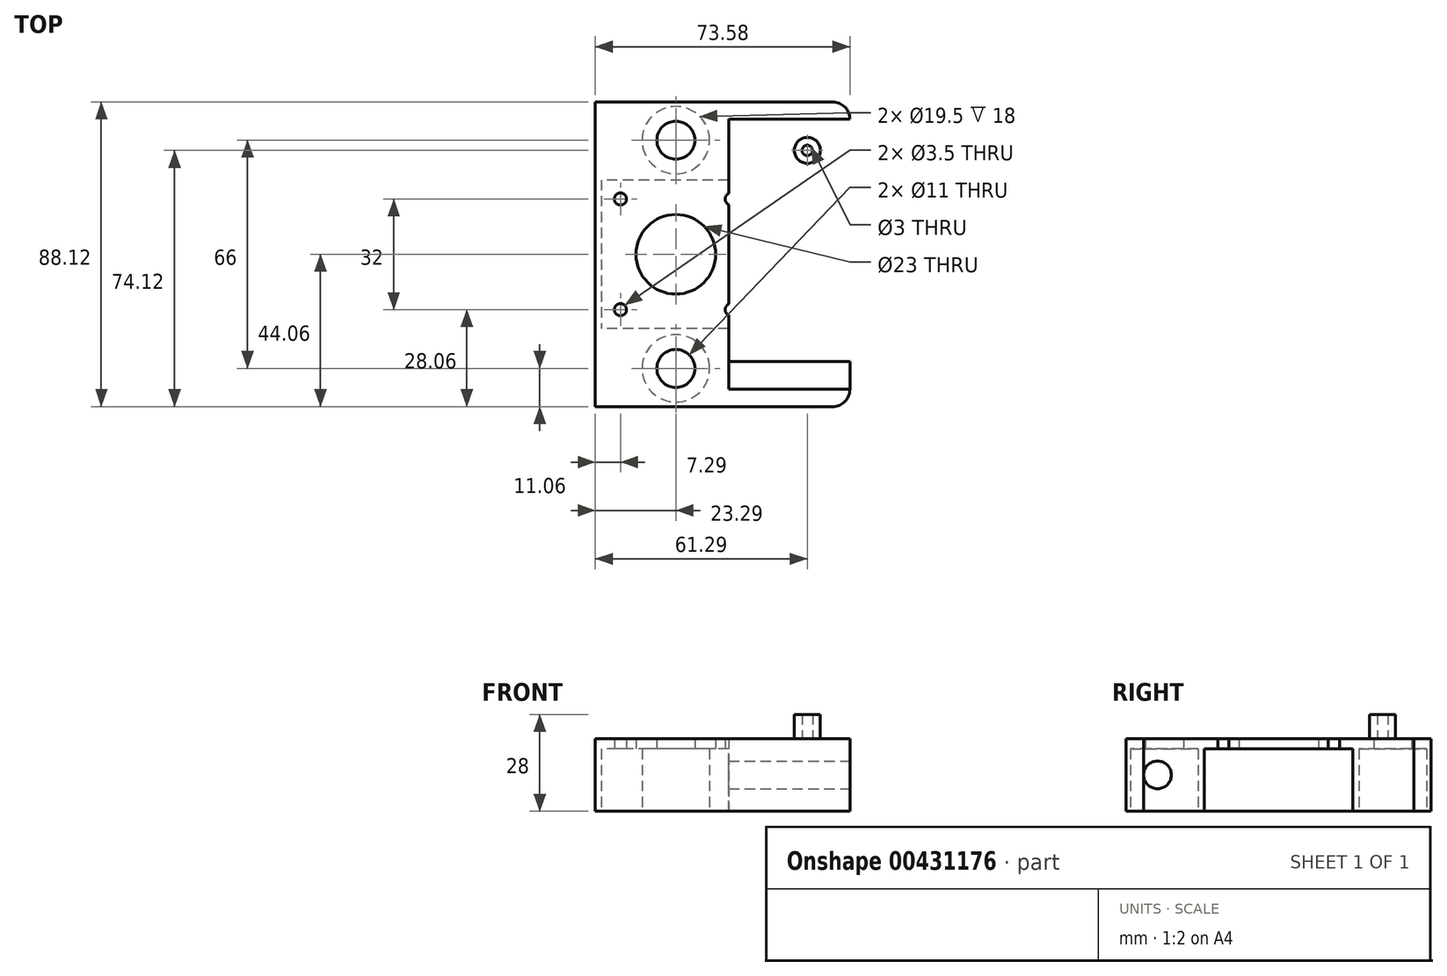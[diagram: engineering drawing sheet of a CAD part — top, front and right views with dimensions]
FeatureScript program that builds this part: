
annotation { "Feature Type Name" : "Feature", "Feature Type Description" : "" }
export const myFeature = defineFeature(function(context is Context, id is Id, definition is map)
    precondition{}
    {
        {
            var Q0;
            Q0=qCreatedBy(makeId("Top.planeOp"),FACE);
            var sketch = newSketch(context, id + "F0", { "sketchPlane" : qUnion([Q0])});
            skLineSegment(sketch, "E0", {"start": v(26.75, 0) * mm, "end": v(38, 0) * mm});
            skCircle(sketch, "E1", {"center": v(38, 0) * mm, "radius": 11.25 * mm});
            skLineSegment(sketch, "E2", {"start": v(0, 0) * mm, "end": v(0, 33) * mm});
            skLineSegment(sketch, "E3", {"start": v(0, 0) * mm, "end": v(0, -33) * mm});
            skLineSegment(sketch, "E4.bottom", {"start": v(0, 27) * mm, "end": v(0, 27) * mm});
            skLineSegment(sketch, "E4.top", {"start": v(0, -27) * mm, "end": v(0, -27) * mm});
            skCircle(sketch, "E5", {"center": v(0, -33) * mm, "radius": 9.75 * mm});
            skCircle(sketch, "E6", {"center": v(0, 33) * mm, "radius": 9.75 * mm});
            skLineSegment(sketch, "E7", {"start": v(0, 0) * mm, "end": v(26.75, 0) * mm});
            skLineSegment(sketch, "E8.bottom", {"start": v(21.5, 21.5) * mm, "end": v(21.48, 21.5) * mm});
            skLineSegment(sketch, "E8.top", {"start": v(21.5, -21.5) * mm, "end": v(-21.5, -21.5) * mm});
            skLineSegment(sketch, "E8.left", {"start": v(21.5, 21.5) * mm, "end": v(21.5, 0) * mm});
            skLineSegment(sketch, "E8.right", {"start": v(-21.5, 21.5) * mm, "end": v(-21.5, -21.5) * mm});
            skPoint(sketch, "E8.middle", {"position": v(0, 0) * mm});
            skLineSegment(sketch, "E9", {"start": v(21.5, 0) * mm, "end": v(21.5, -21.5) * mm});
            skLineSegment(sketch, "E10.bottom", {"start": v(23.3, 44.06) * mm, "end": v(-23.3, 44.06) * mm});
            skLineSegment(sketch, "E10.top", {"start": v(23.3, -44.06) * mm, "end": v(-23.3, -44.06) * mm});
            skLineSegment(sketch, "E10.right", {"start": v(-23.3, 44.06) * mm, "end": v(-23.3, -44.06) * mm});
            skLineSegment(sketch, "E11", {"start": v(21.48, 21.5) * mm, "end": v(-21.5, 21.5) * mm});
            skLineSegment(sketch, "E12.right", {"start": v(50.3, 23.56) * mm, "end": v(50.3, -23.56) * mm});
            skLineSegment(sketch, "E13.bottom", {"start": v(-23.3, 44.06) * mm, "end": v(23.3, 44.06) * mm});
            skLineSegment(sketch, "E13.top", {"start": v(-23.3, -44.06) * mm, "end": v(23.3, -44.06) * mm});
            skCircle(sketch, "E14", {"center": v(0, 33) * mm, "radius": 5.5 * mm});
            skCircle(sketch, "E15", {"center": v(0, -33) * mm, "radius": 5.5 * mm});
            skLineSegment(sketch, "E16", {"start": v(23.3, -44.06) * mm, "end": v(45.3, -44.06) * mm});
            skLineSegment(sketch, "E17", {"start": v(50.3, -39.06) * mm, "end": v(50.3, -23.56) * mm});
            skLineSegment(sketch, "E18", {"start": v(23.3, 44.06) * mm, "end": v(45.3, 44.06) * mm});
            skLineSegment(sketch, "E19", {"start": v(50.3, 39.06) * mm, "end": v(50.3, 23.56) * mm});
            skPoint(sketch, "E20.visualSharp", {"position": v(50.3, -44.06) * mm});
            skArc(sketch, "E20.filletArc", {"start": v(45.3, -44.06) * mm, "mid": v(48.83, -42.6) * mm, "end": v(50.3, -39.06) * mm});
            skPoint(sketch, "E21.visualSharp", {"position": v(50.3, 44.06) * mm});
            skArc(sketch, "E21.filletArc", {"start": v(50.3, 39.06) * mm, "mid": v(48.83, 42.6) * mm, "end": v(45.3, 44.06) * mm});
            skSolve(sketch);
        }
        {
            var Q0;
            Q0=makeQuery(id+"F0.imprint","IMPRINT",FACE,{"disambiguationData":[TD([[makeQuery(id+"F0.imprint","IMPRINT",EDGE,{"derivedFrom":sQuery(id+"F0.wireOp",EDGE,"E1")}),-1.0]])]});
            var Q1;
            Q1=makeQuery(id+"F0.imprint","IMPRINT",FACE,{"disambiguationData":[TD([[makeQuery(id+"F0.imprint","IMPRINT",EDGE,{"derivedFrom":sQuery(id+"F0.wireOp",EDGE,"7569d964-31c0-40f6-a892-1a6ad66e8234")}),-1.0]])]});
            var Q2;
            Q2=makeQuery(id+"F0.imprint","IMPRINT",FACE,{"disambiguationData":[TD([[makeQuery(id+"F0.imprint","IMPRINT",EDGE,{"derivedFrom":sQuery(id+"F0.wireOp",EDGE,"e01d2da0-1d26-4bb3-a429-6a2a41ea2c41")}),1.0]])]});
            var Q3;
            Q3=makeQuery(id+"F0.imprint","IMPRINT",FACE,{"disambiguationData":[TD([[makeQuery(id+"F0.imprint","IMPRINT",EDGE,{"derivedFrom":sQuery(id+"F0.wireOp",EDGE,"7569d964-31c0-40f6-a892-1a6ad66e8234")}),1.0]])]});
            var Q4;
            Q4=makeQuery(id+"F0.imprint","IMPRINT",FACE,{"disambiguationData":[TD([[makeQuery(id+"F0.imprint","IMPRINT",EDGE,{"derivedFrom":sQuery(id+"F0.wireOp",EDGE,"E5")}),-1.0]])]});
            extrude(context, id + "F1", {"entities" : qUnion([Q0, Q1, Q2, Q3, Q4]), "depth" : 2 * mm});
        }
        {
            var Q0;
            Q0=makeQuery(id+"F1.opExtrude","CAP_FACE",FACE,{"disambiguationData":[OSD([sQuery(id+"F0.wireOp",EDGE,"E1"),sQuery(id+"F0.wireOp",EDGE,"7569d964-31c0-40f6-a892-1a6ad66e8234"),sQuery(id+"F0.wireOp",EDGE,"e01d2da0-1d26-4bb3-a429-6a2a41ea2c41"),sQuery(id+"F0.wireOp",EDGE,"E8.bottom"),sQuery(id+"F0.wireOp",EDGE,"E8.top"),sQuery(id+"F0.wireOp",EDGE,"E8.left"),sQuery(id+"F0.wireOp",EDGE,"E8.right"),sQuery(id+"F0.wireOp",EDGE,"E9"),sQuery(id+"F0.wireOp",EDGE,"E11"),sQuery(id+"F0.wireOp",EDGE,"E12.right"),sQuery(id+"F0.wireOp",EDGE,"618431a0-3797-4b71-b07f-beab4b43895c"),sQuery(id+"F0.wireOp",EDGE,"eef4be6b-fde0-4edc-b3ba-83a9abe2952a"),sQuery(id+"F0.wireOp",EDGE,"E13.bottom"),sQuery(id+"F0.wireOp",EDGE,"E13.top"),sQuery(id+"F0.wireOp",EDGE,"E10.right"),sQuery(id+"F0.wireOp",EDGE,"E13.right")])],"isStart":false});
            var sketch = newSketch(context, id + "F2", { "sketchPlane" : qUnion([Q0])});
            skCircle(sketch, "E22", {"center": v(38, 0) * mm, "radius": 5.1 * mm});
            skLineSegment(sketch, "E23", {"start": v(38, 0) * mm, "end": v(38, 8) * mm});
            skCircle(sketch, "E24", {"center": v(38, 8) * mm, "radius": 2 * mm});
            skCircle(sketch, "E25.MirrorC", {"center": v(38, -8) * mm, "radius": 2 * mm});
            skLineSegment(sketch, "E26", {"start": v(38, 0) * mm, "end": v(46, 0) * mm});
            skCircle(sketch, "E27", {"center": v(46, 0) * mm, "radius": 2 * mm});
            skCircle(sketch, "E28.MirrorC", {"center": v(30, 0) * mm, "radius": 2 * mm});
            skCircle(sketch, "E29", {"center": v(0, -33) * mm, "radius": 9.75 * mm});
            skCircle(sketch, "E30", {"center": v(0, 33) * mm, "radius": 9.75 * mm});
            skSolve(sketch);
        }
        {
            var Q0;
            Q0=makeQuery(id+"F2.imprint","IMPRINT",FACE,{"disambiguationData":[TD([[makeQuery(id+"F2.imprint","IMPRINT",EDGE,{"derivedFrom":sQuery(id+"F2.wireOp",EDGE,"E29")}),-1.0]])]});
            var Q1;
            Q1=makeQuery(id+"F2.imprint","IMPRINT",FACE,{"disambiguationData":[TD([[makeQuery(id+"F2.imprint","IMPRINT",EDGE,{"derivedFrom":sQuery(id+"F2.wireOp",EDGE,"E24")}),-1.0]])]});
            extrude(context, id + "F3", {"entities" : qUnion([Q0, Q1]), "operationType" : NewBodyOperationType.ADD, "depth" : 16 * mm});
        }
        {
            var Q0;
            Q0=makeQuery(id+"F3.opExtrude","CAP_FACE",FACE,{"disambiguationData":[OSD([sQuery(id+"F0.wireOp",EDGE,"E8.bottom"),sQuery(id+"F0.wireOp",EDGE,"E8.top"),sQuery(id+"F0.wireOp",EDGE,"E8.left"),sQuery(id+"F0.wireOp",EDGE,"E8.right"),sQuery(id+"F0.wireOp",EDGE,"E9"),sQuery(id+"F0.wireOp",EDGE,"E11"),sQuery(id+"F0.wireOp",EDGE,"E12.right"),sQuery(id+"F0.wireOp",EDGE,"618431a0-3797-4b71-b07f-beab4b43895c"),sQuery(id+"F0.wireOp",EDGE,"eef4be6b-fde0-4edc-b3ba-83a9abe2952a"),sQuery(id+"F0.wireOp",EDGE,"E13.bottom"),sQuery(id+"F0.wireOp",EDGE,"E13.top"),sQuery(id+"F0.wireOp",EDGE,"E10.right"),sQuery(id+"F0.wireOp",EDGE,"E13.right"),sQuery(id+"F2.wireOp",EDGE,"E22"),sQuery(id+"F2.wireOp",EDGE,"E24"),sQuery(id+"F2.wireOp",EDGE,"E25.MirrorC"),sQuery(id+"F2.wireOp",EDGE,"E27"),sQuery(id+"F2.wireOp",EDGE,"E28.MirrorC"),sQuery(id+"F2.wireOp",EDGE,"E29"),sQuery(id+"F2.wireOp",EDGE,"E30")])],"isStart":false});
            var sketch = newSketch(context, id + "F4", { "sketchPlane" : qUnion([Q0])});
            skCircle(sketch, "E31", {"center": v(0, 0) * mm, "radius": 11.5 * mm});
            skLineSegment(sketch, "E32", {"start": v(0, 0) * mm, "end": v(16, 0) * mm, "construction": true});
            skPoint(sketch, "E32.endSnap0", {"position": v(21.5, 0) * mm});
            skLineSegment(sketch, "E33", {"start": v(16, 0) * mm, "end": v(16, 16) * mm, "construction": true});
            skCircle(sketch, "E34", {"center": v(16, 16) * mm, "radius": 1.75 * mm});
            skCircle(sketch, "E35.MirrorC", {"center": v(-16, 16) * mm, "radius": 1.75 * mm});
            skCircle(sketch, "E36.MirrorC", {"center": v(16, -16) * mm, "radius": 1.75 * mm});
            skCircle(sketch, "E37.MirrorC", {"center": v(-16, -16) * mm, "radius": 1.75 * mm});
            skSolve(sketch);
        }
        {
            var Q0;
            Q0=makeQuery(id+"F4.imprint","IMPRINT",FACE,{"disambiguationData":[TD([[makeQuery(id+"F4.imprint","IMPRINT",EDGE,{"derivedFrom":makeQuery(id+"F3.opExtrude","CAP_EDGE",EDGE,{"disambiguationData":[OSD([sQuery(id+"F2.wireOp",EDGE,"E22")])],"isStart":false})}),-1.0]])]});
            var Q1;
            Q1=makeQuery(id+"F4.imprint","IMPRINT",FACE,{"disambiguationData":[TD([[makeQuery(id+"F4.imprint","IMPRINT",EDGE,{"derivedFrom":sQuery(id+"F4.wireOp",EDGE,"E31")}),-1.0]])]});
            var Q2;
            Q2=makeQuery(id+"F4.imprint","IMPRINT",FACE,{"disambiguationData":[TD([[makeQuery(id+"F4.imprint","IMPRINT",EDGE,{"derivedFrom":makeQuery(id+"F3.opExtrude","CAP_EDGE",EDGE,{"disambiguationData":[OSD([sQuery(id+"F2.wireOp",EDGE,"E29")])],"isStart":false})}),1.0]])]});
            var Q3;
            Q3=makeQuery(id+"F4.imprint","IMPRINT",FACE,{"disambiguationData":[TD([[makeQuery(id+"F4.imprint","IMPRINT",EDGE,{"derivedFrom":makeQuery(id+"F3.opExtrude","CAP_EDGE",EDGE,{"disambiguationData":[OSD([sQuery(id+"F2.wireOp",EDGE,"E30")])],"isStart":false})}),1.0]])]});
            extrude(context, id + "F5", {"entities" : qUnion([Q0, Q1, Q2, Q3]), "operationType" : NewBodyOperationType.ADD, "depth" : 3 * mm});
        }
        {
            var Q0;
            {var subQ0=sQuery(id+"F0.wireOp",EDGE,"E12.right");Q0=makeQuery(id+"F5.boolean.opBoolean","MERGE",FACE,{"derivedFrom":[makeQuery(id+"F3.boolean.opBoolean","MERGE",FACE,{"derivedFrom":[makeQuery(id+"F1.opExtrude","SWEPT_FACE",FACE,{"disambiguationData":[OSD([subQ0])]}),makeQuery(id+"F3.opExtrude","SWEPT_FACE",FACE,{"disambiguationData":[OSD([subQ0])]})]}),makeQuery(id+"F5.opExtrude","SWEPT_FACE",FACE,{"disambiguationData":[OSD([subQ0])]})]});}
            var sketch = newSketch(context, id + "F6", { "sketchPlane" : qUnion([Q0])});
            skLineSegment(sketch, "E38", {"start": v(0, 0) * mm, "end": v(0, 10.5) * mm, "construction": true});
            skLineSegment(sketch, "E39", {"start": v(0, 10.5) * mm, "end": v(35, 10.5) * mm, "construction": true});
            skPoint(sketch, "E39.endSnap0", {"position": v(-39.06, 10.5) * mm});
            skCircle(sketch, "E40", {"center": v(35, 10.5) * mm, "radius": 4 * mm});
            skCircle(sketch, "E41.MirrorC", {"center": v(-35, 10.5) * mm, "radius": 4 * mm});
            skSolve(sketch);
        }
        {
            var Q0;
            Q0=makeQuery(id+"F0.imprint","IMPRINT",FACE,{"disambiguationData":[TD([[makeQuery(id+"F0.imprint","IMPRINT",EDGE,{"derivedFrom":sQuery(id+"F0.wireOp",EDGE,"E15")}),1.0]])]});
            var Q1;
            Q1=makeQuery(id+"F0.imprint","IMPRINT",FACE,{"disambiguationData":[TD([[makeQuery(id+"F0.imprint","IMPRINT",EDGE,{"derivedFrom":sQuery(id+"F0.wireOp",EDGE,"E14")}),1.0]])]});
            extrude(context, id + "F7", {"entities" : qUnion([Q0, Q1]), "operationType" : NewBodyOperationType.REMOVE, "oppositeDirection" : true, "depth" : -40 * mm});
        }
        {
            var Q0;
            Q0=makeQuery(id+"F6.imprint","IMPRINT",FACE,{"disambiguationData":[TD([[makeQuery(id+"F6.imprint","IMPRINT",EDGE,{"derivedFrom":sQuery(id+"F6.wireOp",EDGE,"E40")}),1.0]])]});
            var Q1;
            Q1=makeQuery(id+"F6.imprint","IMPRINT",FACE,{"disambiguationData":[TD([[makeQuery(id+"F6.imprint","IMPRINT",EDGE,{"derivedFrom":sQuery(id+"F6.wireOp",EDGE,"E41.MirrorC")}),-1.0]])]});
            extrude(context, id + "F8", {"entities" : qUnion([Q0, Q1]), "operationType" : NewBodyOperationType.REMOVE, "oppositeDirection" : true, "depth" : 35 * mm});
        }
        {
            var Q0;
            Q0=makeQuery(id+"F5.opExtrude","CAP_FACE",FACE,{"disambiguationData":[OSD([sQuery(id+"F0.wireOp",EDGE,"E12.right"),sQuery(id+"F0.wireOp",EDGE,"E13.bottom"),sQuery(id+"F0.wireOp",EDGE,"E13.top"),sQuery(id+"F0.wireOp",EDGE,"E10.right"),sQuery(id+"F0.wireOp",EDGE,"E16"),sQuery(id+"F0.wireOp",EDGE,"E17"),sQuery(id+"F0.wireOp",EDGE,"E18"),sQuery(id+"F0.wireOp",EDGE,"E19"),sQuery(id+"F0.wireOp",EDGE,"E20.filletArc"),sQuery(id+"F0.wireOp",EDGE,"E21.filletArc"),sQuery(id+"F2.wireOp",EDGE,"E22"),sQuery(id+"F2.wireOp",EDGE,"E24"),sQuery(id+"F2.wireOp",EDGE,"E25.MirrorC"),sQuery(id+"F2.wireOp",EDGE,"E27"),sQuery(id+"F2.wireOp",EDGE,"E28.MirrorC"),sQuery(id+"F4.wireOp",EDGE,"E31"),sQuery(id+"F4.wireOp",EDGE,"E34"),sQuery(id+"F4.wireOp",EDGE,"E35.MirrorC"),sQuery(id+"F4.wireOp",EDGE,"E36.MirrorC"),sQuery(id+"F4.wireOp",EDGE,"E37.MirrorC")])],"isStart":false});
            var sketch = newSketch(context, id + "F9", { "sketchPlane" : qUnion([Q0])});
            skLineSegment(sketch, "E42", {"start": v(-23.3, 44.06) * mm, "end": v(-23.3, 30.06) * mm, "construction": true});
            skLineSegment(sketch, "E43", {"start": v(50.3, 30.06) * mm, "end": v(38, 30.06) * mm, "construction": true});
            skCircle(sketch, "E44", {"center": v(38, 30.06) * mm, "radius": 3.75 * mm});
            skCircle(sketch, "E45", {"center": v(38, 30.06) * mm, "radius": 1.5 * mm});
            skCircle(sketch, "E46.MirrorC", {"center": v(38, -30.06) * mm, "radius": 3.75 * mm});
            skCircle(sketch, "E47.MirrorC", {"center": v(38, -30.06) * mm, "radius": 1.5 * mm});
            skSolve(sketch);
        }
        {
            var Q0;
            Q0=makeQuery(id+"F9.imprint","IMPRINT",FACE,{"disambiguationData":[TD([[makeQuery(id+"F9.imprint","IMPRINT",EDGE,{"derivedFrom":sQuery(id+"F9.wireOp",EDGE,"E44")}),1.0]])]});
            var Q1;
            Q1=makeQuery(id+"F9.imprint","IMPRINT",FACE,{"disambiguationData":[TD([[makeQuery(id+"F9.imprint","IMPRINT",EDGE,{"derivedFrom":sQuery(id+"F9.wireOp",EDGE,"E46.MirrorC")}),-1.0]])]});
            extrude(context, id + "F10", {"entities" : qUnion([Q0, Q1]), "operationType" : NewBodyOperationType.ADD, "depth" : 7 * mm});
        }
    });
